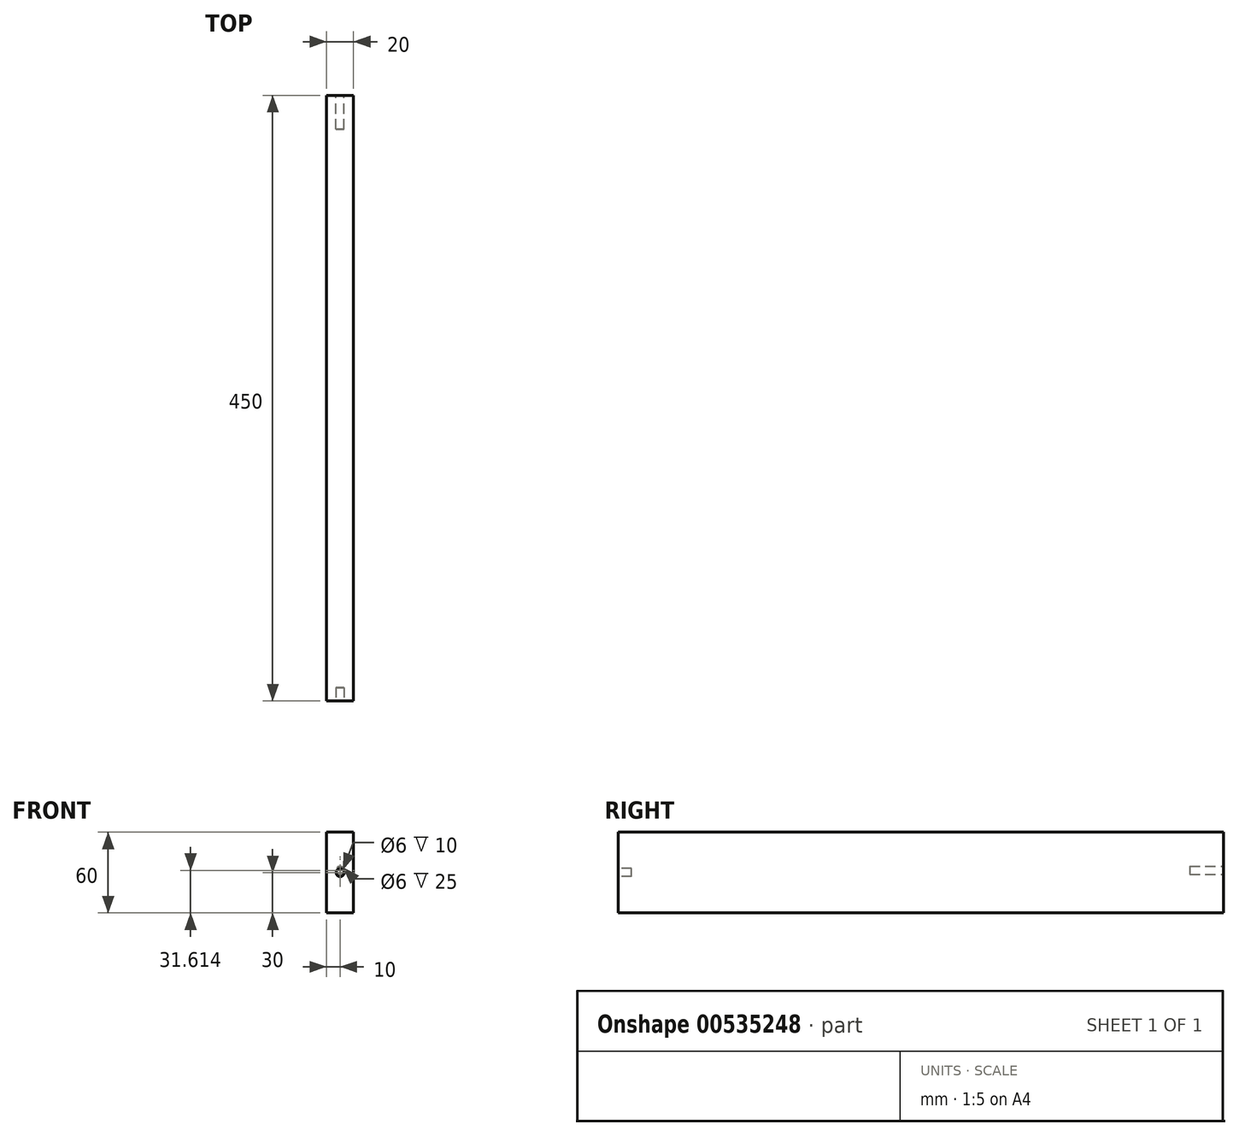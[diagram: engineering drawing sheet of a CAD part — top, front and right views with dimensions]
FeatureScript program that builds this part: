
annotation { "Feature Type Name" : "Feature", "Feature Type Description" : "" }
export const myFeature = defineFeature(function(context is Context, id is Id, definition is map)
    precondition{}
    {
        {
            var Q0;
            Q0=qCreatedBy(makeId("Front.planeOp"),FACE);
            var sketch = newSketch(context, id + "F0", { "sketchPlane" : qUnion([Q0])});
            skLineSegment(sketch, "E0.bottom", {"start": v(0, 0) * mm, "end": v(20, 0) * mm});
            skLineSegment(sketch, "E0.top", {"start": v(0, 60) * mm, "end": v(20, 60) * mm});
            skLineSegment(sketch, "E0.left", {"start": v(0, 0) * mm, "end": v(0, 60) * mm});
            skLineSegment(sketch, "E0.right", {"start": v(20, 0) * mm, "end": v(20, 60) * mm});
            skSolve(sketch);
        }
        {
            var Q0;
            Q0=qSketchRegion(id+"F0",true);
            extrude(context, id + "F1", {"entities" : qUnion([Q0]), "depth" : 450 * mm, "offsetDistance" : 25 * mm, "symmetric" : true});
        }
        {
            var Q0;
            Q0=makeQuery(id+"F1.opExtrude","CAP_FACE",FACE,{"disambiguationData":[OSD([sQuery(id+"F0.wireOp",EDGE,"E0.bottom"),sQuery(id+"F0.wireOp",EDGE,"E0.top"),sQuery(id+"F0.wireOp",EDGE,"E0.left"),sQuery(id+"F0.wireOp",EDGE,"E0.right")])],"isStart":false});
            var sketch = newSketch(context, id + "F2", { "sketchPlane" : qUnion([Q0])});
            skCircle(sketch, "E1", {"center": v(10, 30) * mm, "radius": 3 * mm});
            skPoint(sketch, "E1.centerSnap0", {"position": v(0, 30) * mm});
            skPoint(sketch, "E1.centerSnap1", {"position": v(10, 60) * mm});
            skSolve(sketch);
        }
        {
            var Q0;
            Q0=qSketchRegion(id+"F2",true);
            extrude(context, id + "F3", {"entities" : qUnion([Q0]), "operationType" : NewBodyOperationType.REMOVE, "oppositeDirection" : true, "depth" : 10 * mm, "offsetDistance" : 25 * mm});
        }
        {
            var Q0;
            Q0=makeQuery(id+"F1.opExtrude","CAP_FACE",FACE,{"disambiguationData":[OSD([sQuery(id+"F0.wireOp",EDGE,"E0.bottom"),sQuery(id+"F0.wireOp",EDGE,"E0.top"),sQuery(id+"F0.wireOp",EDGE,"E0.left"),sQuery(id+"F0.wireOp",EDGE,"E0.right")])],"isStart":true});
            var sketch = newSketch(context, id + "F4", { "sketchPlane" : qUnion([Q0])});
            skCircle(sketch, "E2", {"center": v(-10, 31.61) * mm, "radius": 3 * mm});
            skPoint(sketch, "E2.centerSnap0", {"position": v(-10, 60) * mm});
            skSolve(sketch);
        }
        {
            var Q0;
            Q0=qSketchRegion(id+"F4",true);
            extrude(context, id + "F5", {"entities" : qUnion([Q0]), "operationType" : NewBodyOperationType.REMOVE, "oppositeDirection" : true, "depth" : 25 * mm, "offsetDistance" : 25 * mm});
        }
    });
